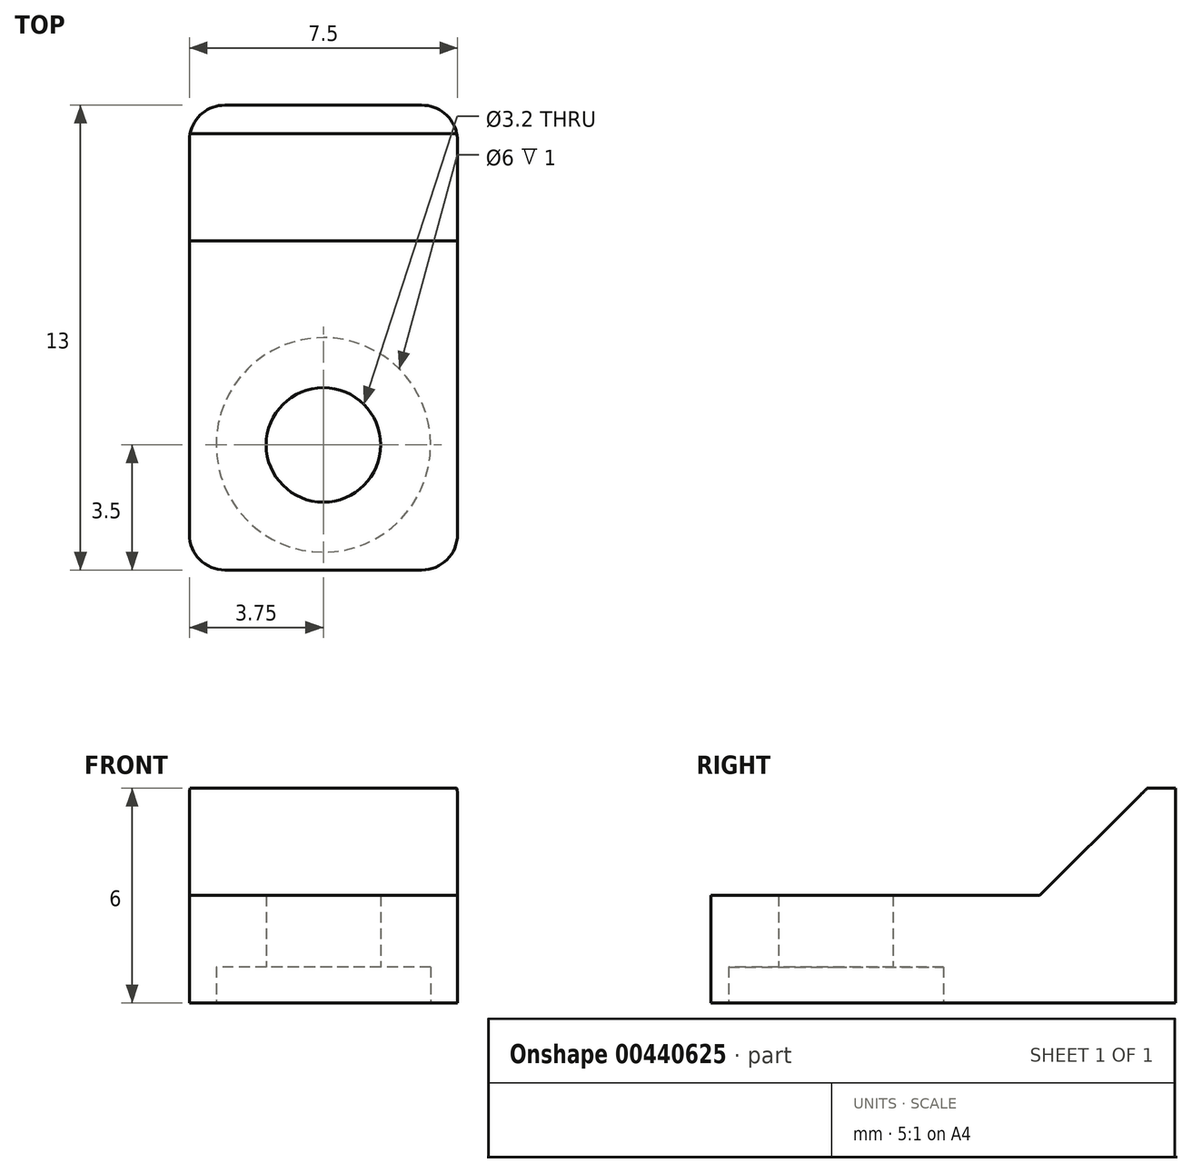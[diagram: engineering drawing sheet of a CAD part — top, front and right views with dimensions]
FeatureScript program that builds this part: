
annotation { "Feature Type Name" : "Feature", "Feature Type Description" : "" }
export const myFeature = defineFeature(function(context is Context, id is Id, definition is map)
    precondition{}
    {
        {
            var Q0;
            Q0=qCreatedBy(makeId("Top.planeOp"),FACE);
            var sketch = newSketch(context, id + "F0", { "sketchPlane" : qUnion([Q0])});
            skLineSegment(sketch, "E0.bottom", {"start": v(3.75, -6.5) * mm, "end": v(-3.75, -6.5) * mm});
            skLineSegment(sketch, "E0.top", {"start": v(3.75, 6.5) * mm, "end": v(-3.75, 6.5) * mm});
            skLineSegment(sketch, "E0.left", {"start": v(3.75, -6.5) * mm, "end": v(3.75, 6.5) * mm});
            skLineSegment(sketch, "E0.right", {"start": v(-3.75, -6.5) * mm, "end": v(-3.75, 6.5) * mm});
            skPoint(sketch, "E0.middle", {"position": v(0, 0) * mm});
            skCircle(sketch, "E1", {"center": v(0, -3) * mm, "radius": 1.6 * mm});
            skCircle(sketch, "E2", {"center": v(0, -3) * mm, "radius": 3 * mm});
            skSolve(sketch);
        }
        {
            var Q0;
            Q0 = qSketchRegion(id + "F0", true);
            var Q1;
            Q1=makeQuery(id+"F0.imprint","IMPRINT",FACE,{"disambiguationData":[TD([[makeQuery(id+"F0.imprint","IMPRINT",EDGE,{"derivedFrom":sQuery(id+"F0.wireOp",EDGE,"E1")}),-1.0]])]});
            extrude(context, id + "F1", {"entities" : qUnion([Q0, Q1]), "depth" : 3 * mm, "offsetDistance" : 25 * mm});
        }
        {
            var Q0;
            Q0=makeQuery(id+"F1.opExtrude","SWEPT_FACE",FACE,{"disambiguationData":[OSD([sQuery(id+"F0.wireOp",EDGE,"E0.left")])]});
            var sketch = newSketch(context, id + "F2", { "sketchPlane" : qUnion([Q0])});
            skLineSegment(sketch, "E3", {"start": v(6.5, 3) * mm, "end": v(6.5, 6) * mm});
            skLineSegment(sketch, "E4", {"start": v(6.5, 6) * mm, "end": v(5.7, 6) * mm});
            skLineSegment(sketch, "E5", {"start": v(5.7, 6) * mm, "end": v(2.7, 3) * mm});
            skSolve(sketch);
        }
        {
            var Q0;
            Q0=makeQuery(id+"F0.imprint","IMPRINT",FACE,{"disambiguationData":[TD([[makeQuery(id+"F0.imprint","IMPRINT",EDGE,{"derivedFrom":sQuery(id+"F0.wireOp",EDGE,"E1")}),-1.0]])]});
            extrude(context, id + "F3", {"entities" : qUnion([Q0]), "operationType" : NewBodyOperationType.REMOVE, "depth" : 1 * mm, "offsetDistance" : 25 * mm});
        }
        {
            var Q0;
            {var subQ0=sQuery(id+"F2.wireOp",EDGE,"E3");Q0=makeQuery(id+"F2.imprint","IMPRINT",FACE,{"disambiguationData":[TD([[makeQuery(id+"F2.imprint","IMPRINT",EDGE,{"derivedFrom":subQ0}),1.0]])]});}
            var Q1;
            Q1=makeQuery(id+"F1.opExtrude","SWEPT_FACE",FACE,{"disambiguationData":[OSD([sQuery(id+"F0.wireOp",EDGE,"E0.right")])]});
            extrude(context, id + "F4", {"entities" : qUnion([Q0]), "operationType" : NewBodyOperationType.ADD, "endBound" : BoundingType.UP_TO_SURFACE, "oppositeDirection" : true, "depth" : 25 * mm, "endBoundEntityFace" : qUnion([Q1]), "offsetDistance" : 25 * mm});
        }
        {
            var Q0;
            Q0=makeQuery(id+"F1.opExtrude","SWEPT_EDGE",EDGE,{"disambiguationData":[OSD([sQuery(id+"F0.wireOp",EDGE,"E0.bottom"),sQuery(id+"F0.wireOp",EDGE,"E0.left")])]});
            var Q1;
            Q1=makeQuery(id+"F1.opExtrude","SWEPT_EDGE",EDGE,{"disambiguationData":[OSD([sQuery(id+"F0.wireOp",EDGE,"E0.bottom"),sQuery(id+"F0.wireOp",EDGE,"E0.right")])]});
            var Q2;
            Q2=makeQuery(id+"F4.boolean.opBoolean","MERGE",EDGE,{"derivedFrom":[makeQuery(id+"F1.opExtrude","SWEPT_EDGE",EDGE,{"disambiguationData":[OSD([sQuery(id+"F0.wireOp",EDGE,"E0.top"),sQuery(id+"F0.wireOp",EDGE,"E0.left")])]}),makeQuery(id+"F4.opExtrude","CAP_EDGE",EDGE,{"disambiguationData":[OSD([sQuery(id+"F2.wireOp",EDGE,"E3")])],"isStart":true})]});
            var Q3;
            {var subQ0=sQuery(id+"F0.wireOp",EDGE,"E0.right");Q3=makeQuery(id+"F4.boolean.opBoolean","MERGE",EDGE,{"derivedFrom":[makeQuery(id+"F1.opExtrude","SWEPT_EDGE",EDGE,{"disambiguationData":[OSD([sQuery(id+"F0.wireOp",EDGE,"E0.top"),subQ0])]}),makeQuery(id+"F4.opExtrude","TWEAK_EDGE",EDGE,{"derivedFrom":[makeQuery(id+"F1.opExtrude","SWEPT_FACE",FACE,{"disambiguationData":[OSD([subQ0])]}),makeQuery(id+"F2.imprint","IMPRINT",EDGE,{"derivedFrom":sQuery(id+"F2.wireOp",EDGE,"E3")})]})]});}
            fillet(context, id + "F5", {"entities" : qUnion([Q0, Q1, Q2, Q3]), "radius" : 1 * mm, "tangentPropagation" : true, "allowEdgeOverflow" : false});
        }
    });
